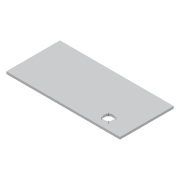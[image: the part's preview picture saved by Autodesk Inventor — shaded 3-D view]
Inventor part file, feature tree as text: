
AUTODESK INVENTOR PART (.ipt)
format: ipt  version: 2016 (Build 200138000, 138)  size: 100,352 bytes
history: native  units: mm
features: sketch x3, extrude x2, hole x1
ambient origin geometry x8: Origin, YZ Plane, XZ Plane, XY Plane, X Axis, Y Axis, Z Axis, Center Point
bodies: Volumenkörper1 (feature_tree)
feature tree (6):
  extrude  "Extrusion1"  Depth=240.0mm
  extrude  "Extrusion3"  Depth=38.0mm
  hole  "Bohrung3"  [1 undecoded]
  sketch  "Skizze1"  dims[d0=500.0mm d1=240.0mm]
  sketch  "Skizze3"  dims[d2=10.0mm d3=0.0mm d32=38.0mm d33=20.0mm d34=50.0mm]
  sketch  "Skizze4"  dims[d35=100.0mm d36=10.0mm d37=0.0mm d38=32.0mm d39=32.0mm d40=2.459mm d41=6.0mm d42=4.0mm d43=2.0mm d44=90.0deg d45=8.0mm d46=20.594885mm]
note: 1 required parameter value undecoded (feature->parameter linkage not recoverable at this tier; creation-order binding heuristic only, values carry confidence <= 0.55)
